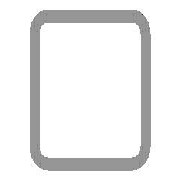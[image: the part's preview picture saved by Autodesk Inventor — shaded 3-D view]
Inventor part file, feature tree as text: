
AUTODESK INVENTOR PART (.ipt)
format: ipt  version: 2025 (Build 290162010, 162A)  size: 132,608 bytes
history: native  units: mm (DEFAULTED — no unit token found)
features: other x4, sketch x1, plane x1
ambient origin geometry x8: Origin, YZ Plane, XZ Plane, XY Plane, X Axis, Y Axis, Z Axis, Center Point
bodies: Solid1 (feature_tree), Body (feature_tree)
feature tree (6):
  parser-record x1  (decoder bookkeeping rows leaked as tree rows — omitted from the tree; the rows remain in map.json)
  other  "Driven Length"
  other  "Start Plane"
  other  "End Plane"
  sketch  "Sketch3"  dims[d3=938.0mm d4=0.0mm d7=4.0mm d9=40.0mm d11=40.0mm d12=2.0mm d13=-0.0mm d14=938.0mm d15=20.0mm d16=20.0mm d17=90.0deg d18=938.0mm]
  plane  "Work Plane3"
